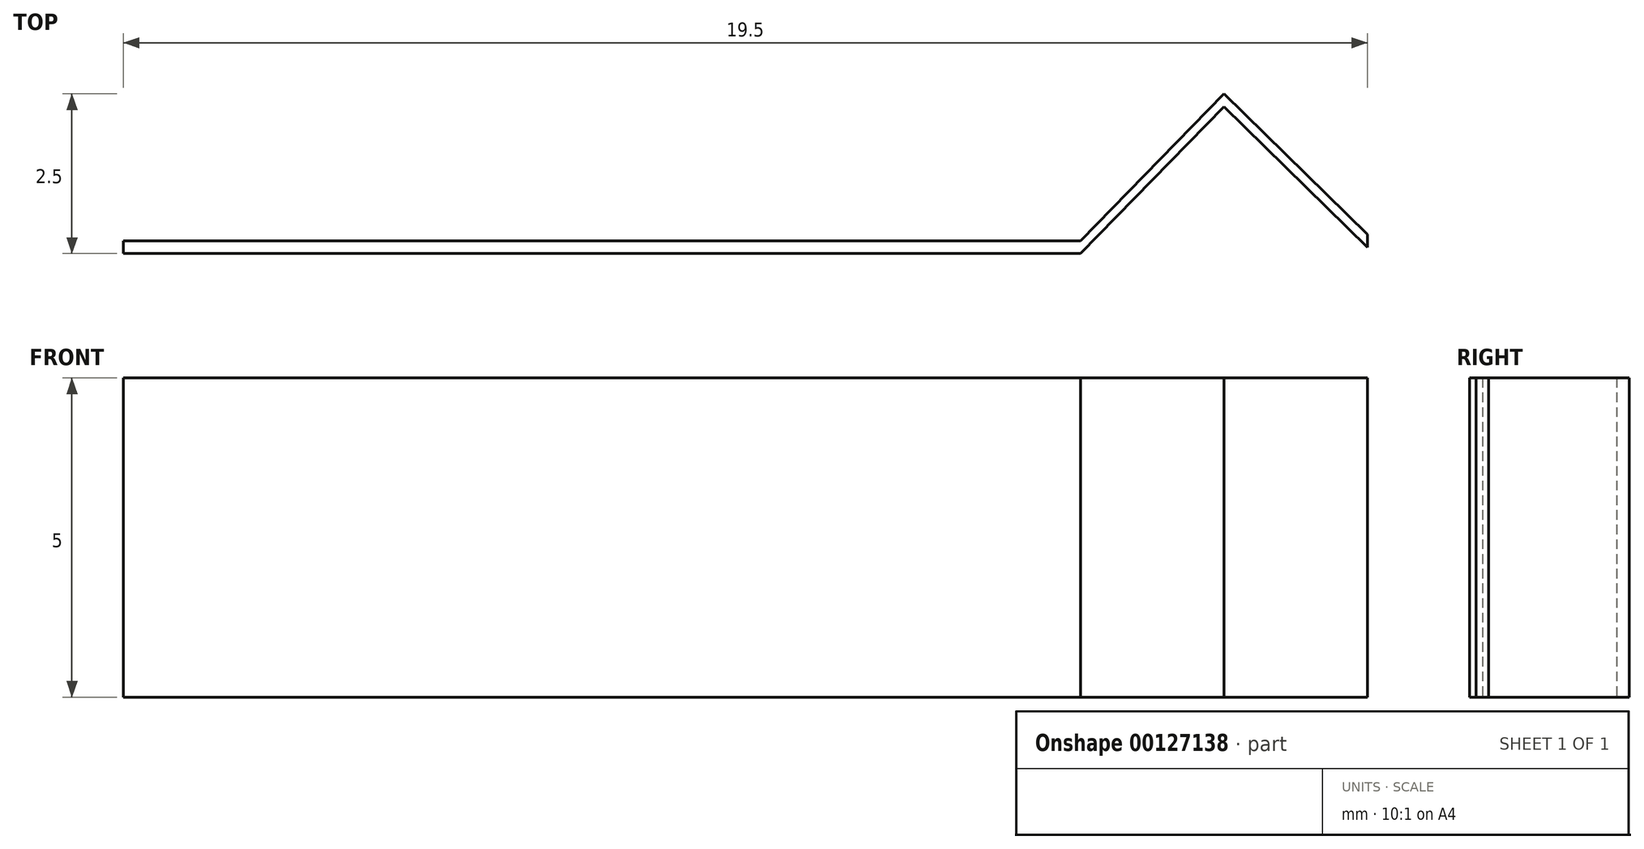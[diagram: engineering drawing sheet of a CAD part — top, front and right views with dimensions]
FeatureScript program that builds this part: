
annotation { "Feature Type Name" : "Feature", "Feature Type Description" : "" }
export const myFeature = defineFeature(function(context is Context, id is Id, definition is map)
    precondition{}
    {
        {
            var Q0;
            Q0=qCreatedBy(makeId("Top.planeOp"),FACE);
            var sketch = newSketch(context, id + "F0", { "sketchPlane" : qUnion([Q0])});
            skLineSegment(sketch, "E0", {"start": v(0, 0) * mm, "end": v(15, 0) * mm});
            skLineSegment(sketch, "E1", {"start": v(15, 0) * mm, "end": v(17.25, 2.3) * mm});
            skLineSegment(sketch, "E2", {"start": v(19.5, 0.3) * mm, "end": v(17.25, 2.5) * mm});
            skLineSegment(sketch, "E3", {"start": v(17.25, 2.5) * mm, "end": v(15, 0.2) * mm});
            skLineSegment(sketch, "E4", {"start": v(15, 0.2) * mm, "end": v(0, 0.2) * mm});
            skLineSegment(sketch, "E5", {"start": v(0, 0.2) * mm, "end": v(0, 0) * mm});
            skLineSegment(sketch, "E6", {"start": v(15, 0.2) * mm, "end": v(15, 0) * mm, "construction": true});
            skLineSegment(sketch, "E7", {"start": v(17.25, 2.5) * mm, "end": v(17.25, 2.3) * mm, "construction": true});
            skLineSegment(sketch, "E8", {"start": v(17.25, 2.3) * mm, "end": v(19.5, 0.1) * mm});
            skLineSegment(sketch, "E9", {"start": v(19.5, 0.1) * mm, "end": v(19.5, 0.3) * mm});
            skSolve(sketch);
        }
        {
            var Q0;
            Q0=makeQuery(id+"F0.imprint","IMPRINT",FACE,{"disambiguationData":[TD([[makeQuery(id+"F0.imprint","IMPRINT",EDGE,{"derivedFrom":sQuery(id+"F0.wireOp",EDGE,"E0")}),1.0]])]});
            extrude(context, id + "F1", {"entities" : qUnion([Q0]), "depth" : 5 * mm});
        }
    });
